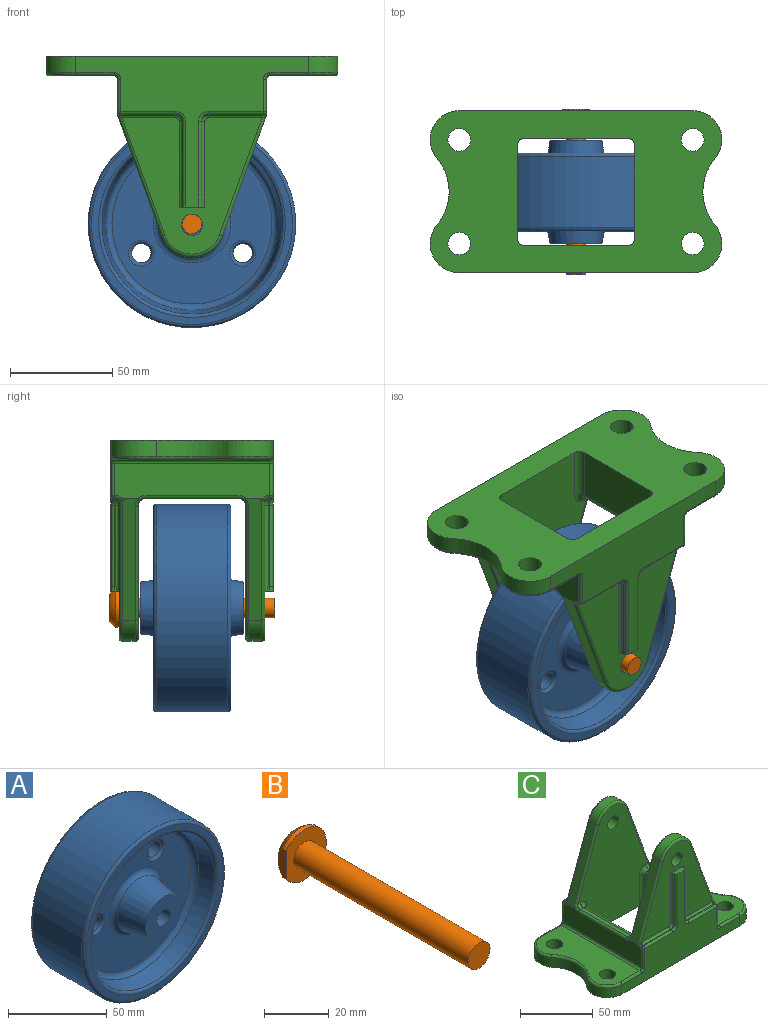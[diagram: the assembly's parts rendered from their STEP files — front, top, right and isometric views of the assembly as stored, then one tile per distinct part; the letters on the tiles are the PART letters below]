
ASSEMBLY  parts=3 mates=2
PART A: 26 faces, bbox 110x50.8x110 mm
  f0: cylinder r=50.8mm len=101.6mm, axis (0,-1,0), area 11147.6mm2, adj f1,f19
  f1: torus R=49.21mm, axis (0,-1,0), area 786.9mm2, adj f0,f2
  f2: plane 98.43x98.43mm, normal (0,-1,0), area 1032.6mm2, adj f1,f3
  f3: torus R=45.75mm, axis (0,-1,0), area 614mm2, adj f2,f4
  f4: cone r=44.19mm half-angle=11.3deg, axis (0,-1,0), area 2630.8mm2, adj f3,f5
  f5: torus R=39.18mm, axis (0,-1,0), area 1124.4mm2, adj f4,f6
  f6: plane 78.37x78.37mm, normal (0,-1,0), area 3306.6mm2, adj f5,f7,f23,f24,f25
  f7: torus R=19.02mm, axis (0,-1,0), area 474.1mm2, adj f6,f8
  f8: cone r=15.9mm half-angle=10.6deg, axis (0,1,0), area 1561.5mm2, adj f7,f9
  f9: plane 25.4x25.4mm, normal (0,-1,0), area 433.5mm2, adj f8,f10
  f10: cylinder r=4.83mm len=50.8mm, axis (0,-1,0), area 1540.4mm2, adj f9,f11
  f11: plane 25.4x25.4mm, normal (0,1,0), area 433.5mm2, adj f10,f12
  f12: cone r=15.49mm half-angle=8.1deg, axis (0,-1,0), area 1744.1mm2, adj f11,f13
  f13: torus R=18.63mm, axis (0,-1,0), area 476.6mm2, adj f12,f14
  f14: plane 77.34x77.34mm, normal (0,1,0), area 3394.4mm2, adj f13,f15,f20,f21,f22
  f15: torus R=38.67mm, axis (0,-1,0), area 1110.5mm2, adj f14,f16
  f16: cone r=44.19mm half-angle=11.3deg, axis (0,1,0), area 3318.4mm2, adj f15,f17
  f17: torus R=45.75mm, axis (0,-1,0), area 614mm2, adj f16,f18
  f18: plane 98.43x98.43mm, normal (0,1,0), area 1032.6mm2, adj f17,f19
  f19: torus R=49.21mm, axis (0,-1,0), area 786.9mm2, adj f0,f18
  f20: cylinder r=4.76mm len=9.53mm, axis (0,1,0), area 218.9mm2, adj f14,f25
  f21: cylinder r=4.76mm len=9.53mm, axis (0,1,0), area 218.9mm2, adj f14,f24
  f22: cylinder r=4.76mm len=9.53mm, axis (0,1,0), area 218.9mm2, adj f14,f23
  f23: torus R=6.35mm, axis (0,-1,0), area 83.7mm2, adj f6,f22
  f24: torus R=6.35mm, axis (0,-1,0), area 83.7mm2, adj f6,f21
  f25: torus R=6.35mm, axis (0,-1,0), area 83.7mm2, adj f6,f20
PART B: 7 faces, bbox 19.1x81x19.1 mm
  f0: plane 19.05x17.46mm, normal (0,-1,0), area 202.4mm2, adj f2,f4,f6
  f1: sphere r=11.11mm, area 202.5mm2, adj f4,f5,f6
  f2: cylinder r=4.76mm len=76.2mm, axis (0,1,0), area 2280.2mm2, adj f0,f3
  f3: plane 9.53x9.53mm, normal (0,-1,0), area 71.3mm2, adj f2
  f4: cylinder r=9.53mm len=19.05mm, axis (0,-1,0), area 77.3mm2, adj f0,f1,f6
  f5: plane 13.31x13.31mm, normal (0,1,0), area 139.2mm2, adj f1
  f6: plane 10.53x3.64mm, normal (-1,0,0), area 31.6mm2, adj f0,f1,f4
PART C: 151 faces, bbox 146.4x82.9x100.9 mm
  f0: plane 114.3x73.82mm, normal (0,1,0), area 2549.4mm2, adj f1,f8,f12,f38,f70,f71,f72,f73
  f1: cylinder r=14.29mm len=22.44mm, axis (0,0,-1), area 247mm2, adj f0,f2,f8,f135
  f2: cylinder r=25.4mm len=34.49mm, axis (0,0,-1), area 301mm2, adj f1,f3,f8,f136
  f3: cylinder r=14.29mm len=22.44mm, axis (0,0,-1), area 247mm2, adj f2,f4,f8,f138
  f4: plane 114.3x73.82mm, normal (0,-1,0), area 2549.4mm2, adj f3,f8,f10,f44,f63,f64,f65,f66
  f5: cylinder r=5.56mm len=11.11mm, axis (0,0,-1), area 332.5mm2, adj f7,f8
  f6: cylinder r=5.56mm len=11.11mm, axis (0,0,-1), area 332.5mm2, adj f7,f8
  f7: plane 76.2x31.75mm, normal (0,0,1), area 1887.6mm2, adj f5,f6,f135,f136,f137,f138,f140,f141
  f8: plane 142.88x79.38mm, normal (0,0,-1), area 7269.4mm2, adj f0,f1,f2,f3,f4,f5,f6,f10
  f9: plane 76.2x17.47mm, normal (-1,0,0), area 1239.5mm2, adj f30,f49,f112,f113,f114,f120,f122,f123
  f10: cylinder r=14.29mm len=22.44mm, axis (0,0,-1), area 247mm2, adj f4,f8,f11,f147
  f11: cylinder r=25.4mm len=34.49mm, axis (0,0,-1), area 301mm2, adj f8,f10,f12,f145
  f12: cylinder r=14.29mm len=22.44mm, axis (0,0,-1), area 247mm2, adj f0,f8,f11,f143
  f13: cylinder r=5.56mm len=11.11mm, axis (0,0,-1), area 332.5mm2, adj f8,f15
  f14: cylinder r=5.56mm len=11.11mm, axis (0,0,-1), area 332.5mm2, adj f8,f15
  f15: plane 76.2x31.75mm, normal (0,0,1), area 1887.6mm2, adj f13,f14,f143,f144,f145,f147,f148,f149
  f16: plane 26.99x0.86mm, normal (0,0,1), area 21.4mm2, adj f46,f61,f62,f69,f127
  f17: plane 46.04x3.18mm, normal (0,0,1), area 146.2mm2, adj f86,f89,f91,f110
  f18: plane 46.04x3.18mm, normal (0,0,1), area 146.2mm2, adj f92,f95,f98,f113
  f19: plane 26.99x0.86mm, normal (0,0,1), area 21.4mm2, adj f35,f73,f81,f82,f117
  f20: plane 68.49x66.68mm, normal (0,1,0), area 2275mm2, adj f31,f32,f33,f34,f38,f78,f79,f80
  f21: plane 26.99x0.86mm, normal (0,0,1), area 21.4mm2, adj f41,f57,f58,f63,f132
  f22: plane 96.84x67.34mm, normal (0,1,0), area 4352.9mm2, adj f8,f50,f88,f90,f91,f96,f97,f98
  f23: plane 46.04x25.4mm, normal (1,0,0), area 1169.4mm2, adj f8,f93,f95,f96
  f24: plane 96.84x67.34mm, normal (0,-1,0), area 4352.9mm2, adj f8,f31,f85,f86,f87,f92,f93,f94
  f25: plane 46.04x25.4mm, normal (-1,0,0), area 1169.4mm2, adj f8,f85,f88,f89
  f26: plane 76.2x17.47mm, normal (1,0,0), area 1239.5mm2, adj f28,f47,f109,f110,f111,f115,f117,f118
  f27: plane 26.99x0.86mm, normal (0,0,1), area 21.4mm2, adj f40,f72,f77,f78,f122
  f28: plane 59.88x22.07mm, normal (0.94,0,0.34), area 402.6mm2, adj f26,f29,f34,f81,f107,f108,f111,f118
  f29: cylinder r=15.88mm len=29.84mm, axis (0,-1,0), area 246.4mm2, adj f28,f30,f33,f106
  f30: plane 59.88x22.07mm, normal (-0.94,0,0.34), area 402.6mm2, adj f9,f29,f32,f77,f104,f105,f112,f124
  f31: cylinder r=5.16mm len=10.32mm, axis (0,-1,0), area 308.8mm2, adj f20,f24
  f32: cylinder r=1.59mm len=58.9mm, axis (0.34,0,0.94), area 153.4mm2, adj f20,f30,f33,f77
  f33: torus R=14.29mm, axis (0,-1,0), area 93.2mm2, adj f20,f29,f32,f34
  f34: cylinder r=1.59mm len=58.9mm, axis (0.34,0,-0.94), area 153.4mm2, adj f20,f28,f33,f81
  f35: cylinder r=3.17mm len=3.18mm, axis (0,-1,0), area 4mm2, adj f19,f36,f74,f83
  f36: plane 39.69x0.79mm, normal (1,0,0), area 31.5mm2, adj f35,f37,f75,f84
  f37: plane 3.57x2.24mm, normal (1,0,-0.01), area 2.3mm2, adj f36,f38,f76,f84
  f38: plane 12.71x3.97mm, normal (0,0,1), area 37.9mm2, adj f0,f20,f37,f39,f70,f76,f80,f84
  f39: plane 42.07x0.79mm, normal (-1,0,0), area 33.4mm2, adj f38,f40,f70,f80
  f40: cylinder r=3.17mm len=3.18mm, axis (0,-1,0), area 4mm2, adj f27,f39,f71,f79
  f41: cylinder r=3.17mm len=3.18mm, axis (0,1,0), area 4mm2, adj f21,f42,f56,f64
  f42: plane 39.69x0.79mm, normal (1,0,0), area 31.5mm2, adj f41,f43,f55,f65
  f43: plane 3.57x2.24mm, normal (1,0,-0.01), area 2.3mm2, adj f42,f44,f55,f66
  f44: plane 12.71x3.97mm, normal (0,0,1), area 37.9mm2, adj f4,f43,f45,f51,f55,f59,f66,f67
  f45: plane 42.07x0.79mm, normal (-1,0,0), area 33.4mm2, adj f44,f46,f59,f67
  f46: cylinder r=3.17mm len=3.18mm, axis (0,1,0), area 4mm2, adj f16,f45,f60,f68
  f47: plane 59.88x22.07mm, normal (0.94,0,0.34), area 402.6mm2, adj f26,f48,f54,f58,f102,f103,f109,f134
  f48: cylinder r=15.88mm len=29.84mm, axis (0,1,0), area 246.4mm2, adj f47,f49,f53,f101
  f49: plane 59.88x22.07mm, normal (-0.94,0,0.34), area 402.6mm2, adj f9,f48,f52,f62,f99,f100,f114,f128
  f50: cylinder r=5.16mm len=10.32mm, axis (0,1,0), area 308.8mm2, adj f22,f51
  f51: plane 68.49x66.68mm, normal (0,-1,0), area 2275mm2, adj f44,f50,f52,f53,f54,f55,f56,f57
  f52: cylinder r=1.59mm len=58.9mm, axis (0.34,0,0.94), area 153.4mm2, adj f49,f51,f53,f62
  f53: torus R=14.29mm, axis (0,1,0), area 93.2mm2, adj f48,f51,f52,f54
  f54: cylinder r=1.59mm len=58.9mm, axis (0.34,0,-0.94), area 153.4mm2, adj f47,f51,f53,f58
  f55: cylinder r=1.59mm len=42.07mm, axis (0,0,-1), area 104.6mm2, adj f42,f43,f44,f51,f56
  f56: torus R=1.59mm, axis (0,1,0), area 10.2mm2, adj f41,f51,f55,f57
  f57: cylinder r=1.59mm len=26.31mm, axis (-1,0,0), area 65.6mm2, adj f21,f51,f56,f58
  f58: bspline ~3.81x3.38mm, area 3.4mm2, adj f21,f47,f54,f57,f133
  f59: cylinder r=1.59mm len=42.07mm, axis (0,0,1), area 104.9mm2, adj f44,f45,f51,f60
  f60: torus R=1.59mm, axis (0,1,0), area 10.2mm2, adj f46,f51,f59,f61
  f61: cylinder r=1.59mm len=26.31mm, axis (-1,0,0), area 65.6mm2, adj f16,f51,f60,f62
  f62: bspline ~3.81x3.38mm, area 3.4mm2, adj f16,f49,f52,f61,f129
  f63: cylinder r=1.59mm len=26.99mm, axis (-1,0,0), area 67.3mm2, adj f4,f21,f64,f131
  f64: torus R=4.76mm, axis (0,1,0), area 14.7mm2, adj f4,f41,f63,f65
  f65: cylinder r=1.59mm len=39.69mm, axis (0,0,1), area 99mm2, adj f4,f42,f64,f66
  f66: cylinder r=1.59mm len=2.4mm, axis (0.01,0,1), area 5.9mm2, adj f4,f43,f44,f65
  f67: cylinder r=1.59mm len=42.07mm, axis (0,0,-1), area 104.9mm2, adj f4,f44,f45,f68
  f68: torus R=4.76mm, axis (0,1,0), area 14.7mm2, adj f4,f46,f67,f69
  f69: cylinder r=1.59mm len=26.99mm, axis (-1,0,0), area 67.3mm2, adj f4,f16,f68,f126
  f70: cylinder r=1.59mm len=42.07mm, axis (0,0,1), area 104.9mm2, adj f0,f38,f39,f71
  f71: torus R=4.76mm, axis (0,1,0), area 14.7mm2, adj f0,f40,f70,f72
  f72: cylinder r=1.59mm len=26.99mm, axis (1,0,0), area 67.3mm2, adj f0,f27,f71,f121
  f73: cylinder r=1.59mm len=26.99mm, axis (1,0,0), area 67.3mm2, adj f0,f19,f74,f116
  f74: torus R=4.76mm, axis (0,1,0), area 14.7mm2, adj f0,f35,f73,f75
  f75: cylinder r=1.59mm len=39.69mm, axis (0,0,-1), area 99mm2, adj f0,f36,f74,f76
  f76: cylinder r=1.59mm len=2.4mm, axis (-0.01,0,-1), area 5.9mm2, adj f0,f37,f38,f75
  f77: bspline ~3.81x3.38mm, area 3.4mm2, adj f27,f30,f32,f78,f123
  f78: cylinder r=1.59mm len=26.31mm, axis (-1,0,0), area 65.6mm2, adj f20,f27,f77,f79
  f79: torus R=1.59mm, axis (0,-1,0), area 10.2mm2, adj f20,f40,f78,f80
  f80: cylinder r=1.59mm len=42.07mm, axis (0,0,1), area 104.9mm2, adj f20,f38,f39,f79
  f81: bspline ~3.81x3.38mm, area 3.4mm2, adj f19,f28,f34,f82,f119
  f82: cylinder r=1.59mm len=26.31mm, axis (-1,0,0), area 65.6mm2, adj f19,f20,f81,f83
  f83: torus R=1.59mm, axis (0,-1,0), area 10.2mm2, adj f20,f35,f82,f84
  f84: cylinder r=1.59mm len=42.07mm, axis (0,0,-1), area 104.6mm2, adj f20,f36,f37,f38,f83
  f85: cylinder r=3.17mm len=25.4mm, axis (0,0,1), area 126.7mm2, adj f8,f24,f25,f87
  f86: cylinder r=3.17mm len=3.18mm, axis (1,0,0), area 14.2mm2, adj f17,f24,f87,f108,f111
  f87: torus R=6.35mm, axis (0,-1,0), area 33.9mm2, adj f24,f85,f86,f89
  f88: cylinder r=3.17mm len=25.4mm, axis (0,0,-1), area 126.7mm2, adj f8,f22,f25,f90
  f89: cylinder r=3.17mm len=46.04mm, axis (0,1,0), area 229.6mm2, adj f17,f25,f87,f90
  f90: torus R=6.35mm, axis (0,-1,0), area 33.9mm2, adj f22,f88,f89,f91
  f91: cylinder r=3.17mm len=3.18mm, axis (-1,0,0), area 14.2mm2, adj f17,f22,f90,f103,f109
  f92: cylinder r=3.17mm len=3.18mm, axis (1,0,0), area 14.2mm2, adj f18,f24,f94,f104,f112
  f93: cylinder r=3.17mm len=25.4mm, axis (0,0,-1), area 126.7mm2, adj f8,f23,f24,f94
  f94: torus R=6.35mm, axis (0,-1,0), area 33.9mm2, adj f24,f92,f93,f95
  f95: cylinder r=3.17mm len=46.04mm, axis (0,-1,0), area 229.6mm2, adj f18,f23,f94,f97
  f96: cylinder r=3.17mm len=25.4mm, axis (0,0,1), area 126.7mm2, adj f8,f22,f23,f97
  f97: torus R=6.35mm, axis (0,-1,0), area 33.9mm2, adj f22,f95,f96,f98
  f98: cylinder r=3.17mm len=3.18mm, axis (-1,0,0), area 14.2mm2, adj f18,f22,f97,f99,f114
  f99: bspline ~4.73x3.21mm, area 7.8mm2, adj f49,f98,f100,f114
  f100: cylinder r=1.59mm len=56.22mm, axis (0.34,0,0.94), area 147.7mm2, adj f22,f49,f99,f101
  f101: torus R=14.29mm, axis (0,-1,0), area 93.2mm2, adj f22,f48,f100,f102
  f102: cylinder r=1.59mm len=56.22mm, axis (0.34,0,-0.94), area 147.7mm2, adj f22,f47,f101,f103
  f103: bspline ~3.58x2.79mm, area 7.8mm2, adj f47,f91,f102,f109
  f104: bspline ~3.58x2.79mm, area 7.8mm2, adj f30,f92,f105,f112
  f105: cylinder r=1.59mm len=56.22mm, axis (-0.34,0,-0.94), area 147.7mm2, adj f24,f30,f104,f106
  f106: torus R=14.29mm, axis (0,-1,0), area 93.2mm2, adj f24,f29,f105,f107
  f107: cylinder r=1.59mm len=56.22mm, axis (-0.34,0,0.94), area 147.7mm2, adj f24,f28,f106,f108
  f108: bspline ~4.73x3.21mm, area 7.8mm2, adj f28,f86,f107,f111
  f109: torus R=4.76mm, axis (1,0,0), area 7.4mm2, adj f26,f47,f91,f103,f110
  f110: cylinder r=1.59mm len=46.04mm, axis (0,-1,0), area 114.8mm2, adj f17,f26,f109,f111
  f111: torus R=4.76mm, axis (1,0,0), area 7.4mm2, adj f26,f28,f86,f108,f110
  f112: torus R=4.76mm, axis (-1,0,0), area 7.4mm2, adj f9,f30,f92,f104,f113
  f113: cylinder r=1.59mm len=46.04mm, axis (0,1,0), area 114.8mm2, adj f9,f18,f112,f114
  f114: torus R=4.76mm, axis (-1,0,0), area 7.4mm2, adj f9,f49,f98,f99,f113
  f115: cylinder r=1.59mm len=15.88mm, axis (0,0,-1), area 39.6mm2, adj f0,f26,f116,f146
  f116: sphere r=1.59mm, area 5.4mm2, adj f73,f115,f117
  f117: cylinder r=1.59mm len=1.59mm, axis (0,-1,0), area 2.1mm2, adj f19,f26,f116,f119
  f118: bspline ~2.29x1.03mm, area 0.7mm2, adj f26,f28,f119
  f119: bspline ~3.99x2.34mm, area 6.3mm2, adj f26,f81,f117,f118
  f120: cylinder r=1.59mm len=15.88mm, axis (0,0,-1), area 39.6mm2, adj f0,f9,f121,f139
  f121: sphere r=1.59mm, area 2.5mm2, adj f72,f120,f122
  f122: cylinder r=1.59mm len=1.59mm, axis (0,1,0), area 2.1mm2, adj f9,f27,f121,f123
  f123: bspline ~3.99x2.34mm, area 6.3mm2, adj f9,f77,f122,f124
  f124: bspline ~2.29x1.03mm, area 0.7mm2, adj f9,f30,f123
  f125: cylinder r=1.59mm len=15.88mm, axis (0,0,1), area 39.6mm2, adj f4,f9,f126,f142
  f126: sphere r=1.59mm, area 4mm2, adj f69,f125,f127
  f127: cylinder r=1.59mm len=1.59mm, axis (0,1,0), area 2.1mm2, adj f9,f16,f126,f129
  f128: bspline ~2.63x1.22mm, area 0.7mm2, adj f9,f49,f129
  f129: bspline ~3.99x2.34mm, area 6.3mm2, adj f9,f62,f127,f128
  f130: cylinder r=1.59mm len=15.88mm, axis (0,0,1), area 39.6mm2, adj f4,f26,f131,f150
  f131: sphere r=1.59mm, area 4mm2, adj f63,f130,f132
  f132: cylinder r=1.59mm len=1.59mm, axis (0,-1,0), area 2.1mm2, adj f21,f26,f131,f133
  f133: bspline ~3.99x2.34mm, area 6.3mm2, adj f26,f58,f132,f134
  f134: bspline ~2.29x1.03mm, area 0.7mm2, adj f26,f47,f133
  f135: torus R=12.7mm, axis (0,0,1), area 74.3mm2, adj f1,f7,f136,f137
  f136: torus R=26.99mm, axis (0,0,1), area 96.4mm2, adj f2,f7,f135,f138
  f137: cylinder r=1.59mm len=19.05mm, axis (1,0,0), area 47.5mm2, adj f0,f7,f135,f139
  f138: torus R=12.7mm, axis (0,0,1), area 74.3mm2, adj f3,f7,f136,f140
  f139: torus R=3.17mm, axis (0,1,0), area 8.5mm2, adj f0,f120,f137,f141
  f140: cylinder r=1.59mm len=19.05mm, axis (-1,0,0), area 47.5mm2, adj f4,f7,f138,f142
  f141: cylinder r=1.59mm len=76.2mm, axis (0,-1,0), area 190mm2, adj f7,f9,f139,f142
  f142: torus R=3.17mm, axis (0,1,0), area 8.5mm2, adj f4,f125,f140,f141
  f143: torus R=12.7mm, axis (0,0,1), area 74.3mm2, adj f12,f15,f144,f145
  f144: cylinder r=1.59mm len=19.05mm, axis (1,0,0), area 47.5mm2, adj f0,f15,f143,f146
  f145: torus R=26.99mm, axis (0,0,1), area 96.4mm2, adj f11,f15,f143,f147
  f146: torus R=3.17mm, axis (0,1,0), area 8.5mm2, adj f0,f115,f144,f148
  f147: torus R=12.7mm, axis (0,0,1), area 74.3mm2, adj f10,f15,f145,f149
  f148: cylinder r=1.59mm len=76.2mm, axis (0,-1,0), area 190mm2, adj f15,f26,f146,f150
  f149: cylinder r=1.59mm len=19.05mm, axis (-1,0,0), area 47.5mm2, adj f4,f15,f147,f150
  f150: torus R=3.17mm, axis (0,1,0), area 8.5mm2, adj f4,f130,f148,f149
PLACE A rot(axis=(0,1,0),90deg) t=(-1.56,-9.51,-18.97)mm
PLACE B rot(axis=(0,1,0),90deg) t=(-1.56,51.65,-18.97)mm
PLACE C rot(axis=(0,1,0),180deg) t=(-1.56,15.94,63.09)mm
MATE cylindrical B.f2 <-> A.f0  axis (0,1,0) through (-1.56,13.55,-18.97)mm
MATE fastened B.f0 <-> C.f29  axis (0,-1,0) through (-1.56,51.65,-19.46)mm
